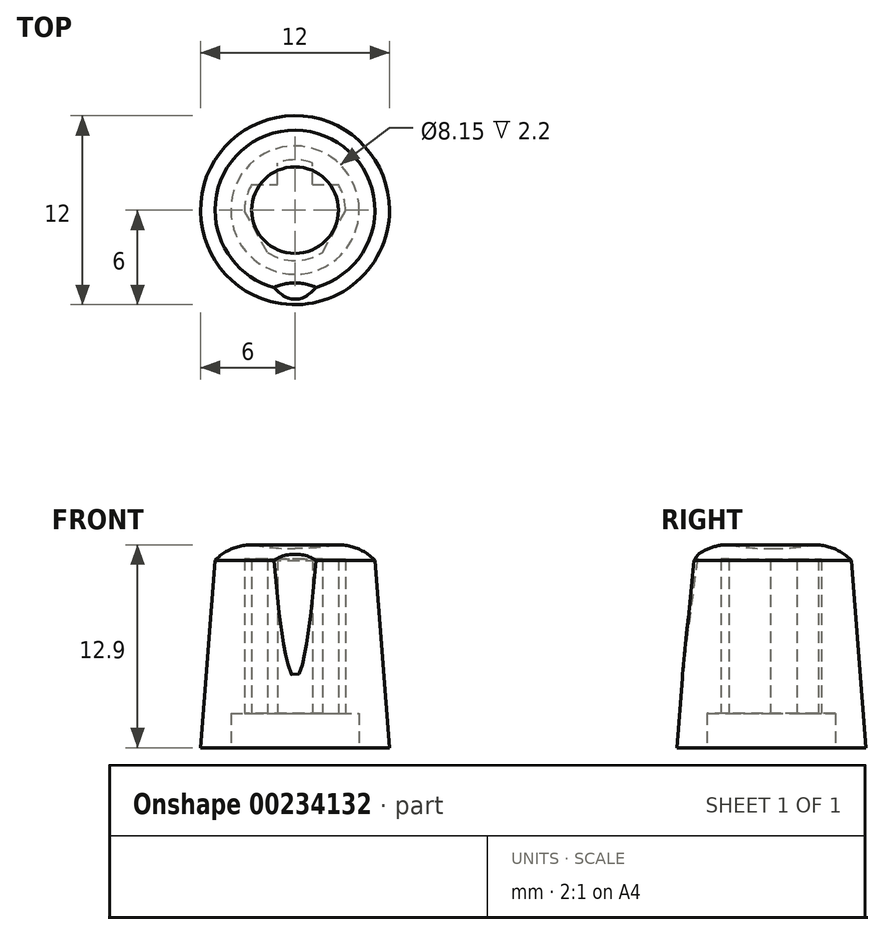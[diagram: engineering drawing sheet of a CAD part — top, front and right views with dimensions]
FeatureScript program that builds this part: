
annotation { "Feature Type Name" : "Feature", "Feature Type Description" : "" }
export const myFeature = defineFeature(function(context is Context, id is Id, definition is map)
    precondition{}
    {
        {
            var Q0;
            Q0=qCreatedBy(makeId("Top.planeOp"),FACE);
            var sketch = newSketch(context, id + "F0", { "sketchPlane" : qUnion([Q0])});
            skCircle(sketch, "E0", {"center": v(0, 0) * mm, "radius": 6 * mm});
            skArc(sketch, "E1", {"start": v(2.58, -1.47) * mm, "mid": v(0, 2.98) * mm, "end": v(-2.58, -1.47) * mm, "construction": true});
            skLineSegment(sketch, "E2", {"start": v(2.58, -1.47) * mm, "end": v(-2.58, -1.47) * mm, "construction": true});
            skSolve(sketch);
        }
        {
            var Q0;
            Q0=qCreatedBy(makeId("Top.planeOp"),FACE);
            cPlane(context, id + "F1", {"entities" : qUnion([Q0]), "cplaneType" : CPlaneType.OFFSET, "offset" : 12.9 * mm, "width" : 150 * mm, "height" : 150 * mm});
        }
        {
            var Q0;
            Q0=qCreatedBy(id+"F1.planeOp",FACE);
            var sketch = newSketch(context, id + "F2", { "sketchPlane" : qUnion([Q0])});
            skCircle(sketch, "E3", {"center": v(0, 0) * mm, "radius": 5 * mm});
            skSolve(sketch);
        }
        {
            var Q0;
            Q0=makeQuery(id+"F2.imprint","IMPRINT",FACE,{"disambiguationData":[TD([[makeQuery(id+"F2.imprint","IMPRINT",EDGE,{"derivedFrom":sQuery(id+"F2.wireOp",EDGE,"E3")}),1.0]])]});
            var Q1;
            Q1=makeQuery(id+"F0.imprint","IMPRINT",FACE,{"disambiguationData":[TD([[makeQuery(id+"F0.imprint","IMPRINT",EDGE,{"derivedFrom":sQuery(id+"F0.wireOp",EDGE,"E0")}),1.0]])]});
            loft(context, id + "F3", {"sheetProfilesArray" : [{ "sheetProfileEntities" : qUnion([Q0]) }, { "sheetProfileEntities" : qUnion([Q1]) }]});
        }
        {
            var Q0;
            Q0=qCreatedBy(makeId("Front.planeOp"),FACE);
            var sketch = newSketch(context, id + "F4", { "sketchPlane" : qUnion([Q0])});
            skLineSegment(sketch, "E4", {"start": v(0, 12.9) * mm, "end": v(0, 12.65) * mm, "construction": true});
            skLineSegment(sketch, "E5", {"start": v(-6, 0) * mm, "end": v(-5, 12.9) * mm});
            skLineSegment(sketch, "E6", {"start": v(5, 12.9) * mm, "end": v(6, 0) * mm});
            skLineSegment(sketch, "E7", {"start": v(0, 12.65) * mm, "end": v(0, 12.9) * mm});
            skLineSegment(sketch, "E8", {"start": v(0, 12.9) * mm, "end": v(2.75, 12.9) * mm});
            skPoint(sketch, "E9.orphan", {"position": v(0, 12.9) * mm});
            skArc(sketch, "E10", {"start": v(0, 12.65) * mm, "mid": v(1.38, 12.71) * mm, "end": v(2.75, 12.9) * mm});
            skArc(sketch, "E11", {"start": v(5.08, 11.9) * mm, "mid": v(4.02, 12.64) * mm, "end": v(2.75, 12.9) * mm});
            skLineSegment(sketch, "E12", {"start": v(5, 12.9) * mm, "end": v(2.75, 12.9) * mm});
            skLineSegment(sketch, "E13", {"start": v(0, 15.7) * mm, "end": v(0, 10.99) * mm, "construction": true});
            skSolve(sketch);
        }
        {
            var Q0;
            Q0=makeQuery(id+"F4.imprint","IMPRINT",FACE,{"disambiguationData":[TD([[makeQuery(id+"F4.imprint","IMPRINT",EDGE,{"derivedFrom":sQuery(id+"F4.wireOp",EDGE,"E7")}),-1.0]])]});
            var Q1;
            {var subQ2=sQuery(id+"F4.wireOp",EDGE,"E11");Q1=makeQuery(id+"F4.imprint","IMPRINT",FACE,{"disambiguationData":[TD([[makeQuery(id+"F4.imprint","IMPRINT",EDGE,{"derivedFrom":subQ2}),-1.0]])]});}
            var Q2;
            Q2=sQuery(id+"F4.wireOp",EDGE,"E13");
            revolve(context, id + "F5", {"operationType" : NewBodyOperationType.REMOVE, "entities" : qUnion([Q0, Q1]), "axis" : qUnion([Q2]), "revolveType" : RevolveType.FULL, "oppositeDirection" : true});
        }
        {
            var Q0;
            Q0=qCreatedBy(makeId("Front.planeOp"),FACE);
            var Q1;
            Q1=sQuery(id+"F4.wireOp",EDGE,"E12");
            cPlane(context, id + "F6", {"entities" : qUnion([Q0, Q1]), "cplaneType" : CPlaneType.LINE_ANGLE, "offset" : 25 * mm, "angle" : 97.5 * degree, "width" : 150 * mm, "height" : 150 * mm});
        }
        {
            var Q0;
            Q0=qCreatedBy(id+"F6.planeOp",FACE);
            var sketch = newSketch(context, id + "F7", { "sketchPlane" : qUnion([Q0])});
            skEllipse(sketch, "E14.0", {"center": v(0, 1.55) * mm, "majorRadius": 5.08 * mm, "minorRadius": 5.03 * mm, "majorAxis": v(-1, 0), "construction": true});
            skCircle(sketch, "E15", {"center": v(0, 10.19) * mm, "radius": 4 * mm});
            skPoint(sketch, "E16", {"position": v(0, 6.59) * mm});
            skSolve(sketch);
        }
        {
            var Q0;
            Q0=makeQuery(id+"F7.imprint","IMPRINT",FACE,{"disambiguationData":[TD([[makeQuery(id+"F7.imprint","IMPRINT",EDGE,{"derivedFrom":sQuery(id+"F7.wireOp",EDGE,"E15")}),1.0]])]});
            extrude(context, id + "F8", {"entities" : qUnion([Q0]), "operationType" : NewBodyOperationType.REMOVE, "depth" : 25 * mm});
        }
        {
            var Q0;
            Q0=makeQuery(id+"F3.opLoft","CAP_FACE",FACE,{"disambiguationData":[OSD([makeQuery(id+"F0.imprint","IMPRINT",FACE,{"disambiguationData":[TD([[makeQuery(id+"F0.imprint","IMPRINT",EDGE,{"derivedFrom":sQuery(id+"F0.wireOp",EDGE,"E0")}),1.0]])]})])],"isStart":true});
            var sketch = newSketch(context, id + "F9", { "sketchPlane" : qUnion([Q0])});
            skCircle(sketch, "E17", {"center": v(0, 0) * mm, "radius": 4.08 * mm});
            skSolve(sketch);
        }
        {
            var Q0;
            Q0=makeQuery(id+"F9.imprint","IMPRINT",FACE,{"disambiguationData":[TD([[makeQuery(id+"F9.imprint","IMPRINT",EDGE,{"derivedFrom":sQuery(id+"F9.wireOp",EDGE,"E17")}),1.0]])]});
            extrude(context, id + "F10", {"entities" : qUnion([Q0]), "operationType" : NewBodyOperationType.REMOVE, "oppositeDirection" : true, "depth" : 2.2 * mm});
        }
        {
            var Q0;
            Q0=makeQuery(id+"F10.boolean.opBoolean","COPY",FACE,{"derivedFrom":makeQuery(id+"F10.opExtrude","CAP_FACE",FACE,{"disambiguationData":[OSD([sQuery(id+"F9.wireOp",EDGE,"E17")])],"isStart":false})});
            var sketch = newSketch(context, id + "F11", { "sketchPlane" : qUnion([Q0])});
            skArc(sketch, "E18", {"start": v(-3.2, 0.05) * mm, "mid": v(-3.1, -0.82) * mm, "end": v(-2.75, -1.64) * mm});
            skLineSegment(sketch, "E19", {"start": v(1.75, 2.68) * mm, "end": v(3.2, 0.05) * mm});
            skLineSegment(sketch, "E20", {"start": v(-2.75, -1.64) * mm, "end": v(-1.1, -1.64) * mm});
            skLineSegment(sketch, "E21", {"start": v(-1.75, 2.68) * mm, "end": v(-3.2, 0.05) * mm});
            skLineSegment(sketch, "E22", {"start": v(0, 7.24) * mm, "end": v(0, -7.07) * mm, "construction": true});
            skArc(sketch, "E23.trimOffspring", {"start": v(1.75, 2.68) * mm, "mid": v(0, 3.2) * mm, "end": v(-1.75, 2.68) * mm});
            skLineSegment(sketch, "E24", {"start": v(1.1, -1.64) * mm, "end": v(1.1, -3) * mm});
            skLineSegment(sketch, "E25", {"start": v(-1.1, -1.64) * mm, "end": v(-1.1, -3) * mm});
            skLineSegment(sketch, "E26.trimOffspring", {"start": v(1.1, -1.64) * mm, "end": v(2.75, -1.64) * mm});
            skArc(sketch, "E27.trimOffspring", {"start": v(2.75, -1.64) * mm, "mid": v(3.1, -0.82) * mm, "end": v(3.2, 0.05) * mm});
            skArc(sketch, "E28.trimOffspring", {"start": v(-1.1, -3) * mm, "mid": v(0, -3.2) * mm, "end": v(1.1, -3) * mm});
            skSolve(sketch);
        }
        {
            var Q0;
            Q0 = qSketchRegion(id + "F11", true);
            extrude(context, id + "F12", {"entities" : qUnion([Q0]), "operationType" : NewBodyOperationType.REMOVE, "oppositeDirection" : true, "depth" : 9.8 * mm});
        }
    });
